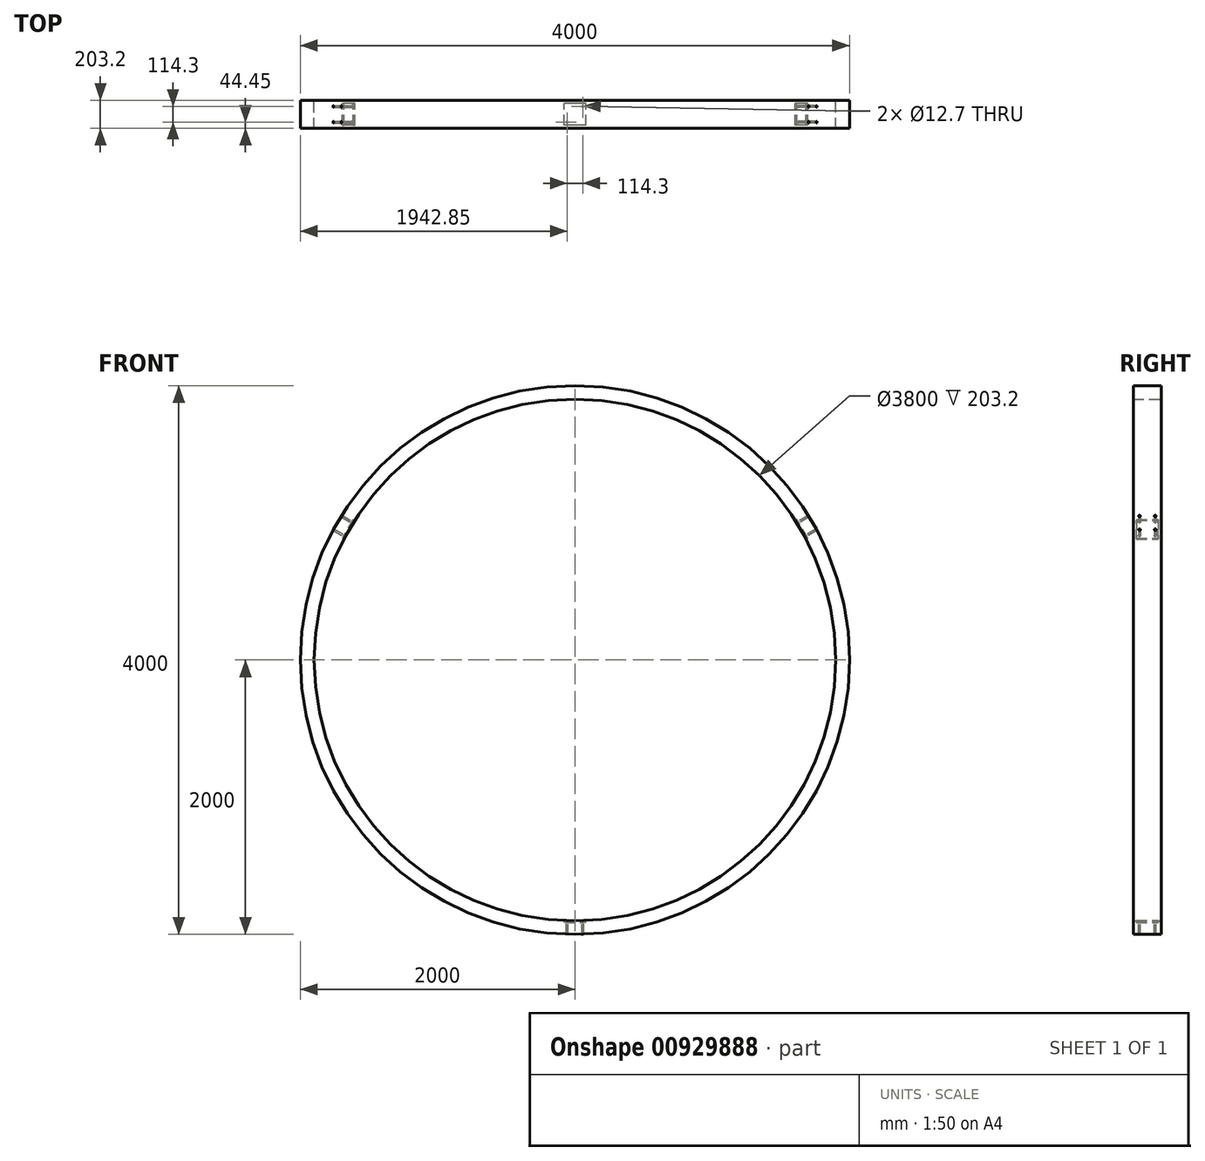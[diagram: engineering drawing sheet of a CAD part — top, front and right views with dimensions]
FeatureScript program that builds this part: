
annotation { "Feature Type Name" : "Feature", "Feature Type Description" : "" }
export const myFeature = defineFeature(function(context is Context, id is Id, definition is map)
    precondition{}
    {
        {
            assignVariable(context, id + "F0", {"name" : "height", "anyValue" : 203.2 * mm});
        }
        {
            var Q0;
            Q0=qCreatedBy(makeId("Front.planeOp"),FACE);
            var sketch = newSketch(context, id + "F1", { "sketchPlane" : qUnion([Q0])});
            skCircle(sketch, "E0", {"center": v(0, 0) * mm, "radius": 1900 * mm});
            skCircle(sketch, "E1", {"center": v(0, 0) * mm, "radius": 2000 * mm});
            skLineSegment(sketch, "E2", {"start": v(0, 0) * mm, "end": v(0, 807.58) * mm, "construction": true});
            skLineSegment(sketch, "E3", {"start": v(0, 1059.46) * mm, "end": v(0, -1141.06) * mm});
            skSolve(sketch);
        }
        {
            var Q0;
            Q0=makeQuery(id+"F1.imprint","IMPRINT",FACE,{"disambiguationData":[TD([[makeQuery(id+"F1.imprint","IMPRINT",EDGE,{"derivedFrom":sQuery(id+"F1.wireOp",EDGE,"E0")}),-1.0]])]});
            extrude(context, id + "F2", {"entities" : qUnion([Q0]), "endBound" : BoundingType.SYMMETRIC, "depth" : getVariable(context, 'height'), "offsetDistance" : 25.4 * mm});
        }
        {
            var Q0;
            Q0=qCreatedBy(makeId("Top.planeOp"),FACE);
            var sketch = newSketch(context, id + "F3", { "sketchPlane" : qUnion([Q0])});
            skLineSegment(sketch, "E4", {"start": v(0, 83.45) * mm, "end": v(0, -223.81) * mm});
            skSolve(sketch);
        }
        {
            var Q0;
            Q0=qCreatedBy(makeId("Top.planeOp"),FACE);
            var Q1;
            Q1=sQuery(id+"F3.wireOp",EDGE,"E4");
            cPlane(context, id + "F4", {"entities" : qUnion([Q0, Q1]), "cplaneType" : CPlaneType.LINE_ANGLE, "offset" : 25.4 * mm, "angle" : 120 * degree, "width" : 152.4 * mm, "height" : 152.4 * mm});
        }
        {
            var Q0;
            Q0=qCreatedBy(makeId("Top.planeOp"),FACE);
            var Q1;
            Q1=sQuery(id+"F3.wireOp",EDGE,"E4");
            cPlane(context, id + "F5", {"entities" : qUnion([Q0, Q1]), "cplaneType" : CPlaneType.LINE_ANGLE, "offset" : 25.4 * mm, "angle" : 240 * degree, "width" : 152.4 * mm, "height" : 152.4 * mm});
        }
        {
            var Q0;
            Q0=qCreatedBy(makeId("Top.planeOp"),FACE);
            var sketch = newSketch(context, id + "F6", { "sketchPlane" : qUnion([Q0])});
            skLineSegment(sketch, "E5.bottom", {"start": v(79.38, -79.38) * mm, "end": v(-79.38, -79.38) * mm});
            skLineSegment(sketch, "E5.top", {"start": v(79.38, 79.38) * mm, "end": v(-79.38, 79.37) * mm});
            skLineSegment(sketch, "E5.left", {"start": v(79.38, -79.38) * mm, "end": v(79.38, 79.38) * mm});
            skLineSegment(sketch, "E5.right", {"start": v(-79.38, -79.38) * mm, "end": v(-79.38, 79.38) * mm});
            skPoint(sketch, "E5.middle", {"position": v(0, 0) * mm});
            skSolve(sketch);
        }
        {
            var Q0;
            Q0=makeQuery(id+"F6.imprint","IMPRINT",FACE,{"disambiguationData":[TD([[makeQuery(id+"F6.imprint","IMPRINT",EDGE,{"derivedFrom":sQuery(id+"F6.wireOp",EDGE,"E5.bottom")}),-1.0]])]});
            var Q1;
            Q1=makeQuery(id+"F2.opExtrude","SWEPT_FACE",FACE,{"disambiguationData":[OSD([sQuery(id+"F1.wireOp",EDGE,"E0")])]});
            extrude(context, id + "F7", {"entities" : qUnion([Q0]), "operationType" : NewBodyOperationType.REMOVE, "endBound" : BoundingType.UP_TO_SURFACE, "oppositeDirection" : true, "depth" : 609.6 * mm, "endBoundEntityFace" : qUnion([Q1]), "hasOffset" : true, "offsetDistance" : 12.7 * mm, "offsetOppositeDirection" : true});
        }
        {
            var Q0;
            Q0=qCreatedBy(id+"F4.planeOp",FACE);
            var sketch = newSketch(context, id + "F8", { "sketchPlane" : qUnion([Q0])});
            skLineSegment(sketch, "E6.bottom", {"start": v(-79.37, -79.37) * mm, "end": v(79.38, -79.37) * mm});
            skLineSegment(sketch, "E6.top", {"start": v(-79.38, 79.38) * mm, "end": v(79.37, 79.38) * mm});
            skLineSegment(sketch, "E6.left", {"start": v(-79.37, -79.37) * mm, "end": v(-79.38, 79.38) * mm});
            skLineSegment(sketch, "E6.right", {"start": v(79.38, -79.37) * mm, "end": v(79.37, 79.38) * mm});
            skPoint(sketch, "E6.middle", {"position": v(0, 0) * mm});
            skSolve(sketch);
        }
        {
            var Q0;
            Q0=qSketchRegion(id+"F8",true);
            var Q1;
            Q1=makeQuery(id+"F2.opExtrude","SWEPT_FACE",FACE,{"disambiguationData":[OSD([sQuery(id+"F1.wireOp",EDGE,"E0")])]});
            extrude(context, id + "F9", {"entities" : qUnion([Q0]), "operationType" : NewBodyOperationType.REMOVE, "endBound" : BoundingType.UP_TO_SURFACE, "depth" : 609.6 * mm, "endBoundEntityFace" : qUnion([Q1]), "hasOffset" : true, "offsetDistance" : 12.7 * mm, "offsetOppositeDirection" : true});
        }
        {
            var Q0;
            Q0=qCreatedBy(id+"F5.planeOp",FACE);
            var sketch = newSketch(context, id + "F10", { "sketchPlane" : qUnion([Q0])});
            skLineSegment(sketch, "E7.bottom", {"start": v(79.38, 79.37) * mm, "end": v(-79.37, 79.37) * mm});
            skLineSegment(sketch, "E7.top", {"start": v(79.37, -79.38) * mm, "end": v(-79.38, -79.38) * mm});
            skLineSegment(sketch, "E7.left", {"start": v(79.38, 79.37) * mm, "end": v(79.37, -79.38) * mm});
            skLineSegment(sketch, "E7.right", {"start": v(-79.37, 79.37) * mm, "end": v(-79.38, -79.38) * mm});
            skPoint(sketch, "E7.middle", {"position": v(0, 0) * mm});
            skSolve(sketch);
        }
        {
            var Q0;
            Q0=qSketchRegion(id+"F10",true);
            var Q1;
            Q1=makeQuery(id+"F2.opExtrude","SWEPT_FACE",FACE,{"disambiguationData":[OSD([sQuery(id+"F1.wireOp",EDGE,"E0")])]});
            extrude(context, id + "F11", {"entities" : qUnion([Q0]), "operationType" : NewBodyOperationType.REMOVE, "endBound" : BoundingType.UP_TO_SURFACE, "depth" : 609.6 * mm, "endBoundEntityFace" : qUnion([Q1]), "hasOffset" : true, "offsetDistance" : 12.7 * mm, "offsetOppositeDirection" : true});
        }
        {
            var Q0;
            Q0=qCreatedBy(id+"F4.planeOp",FACE);
            var sketch = newSketch(context, id + "F12", { "sketchPlane" : qUnion([Q0])});
            skCircle(sketch, "E8", {"center": v(57.15, -57.15) * mm, "radius": 6.35 * mm});
            skCircle(sketch, "E9.MirrorC", {"center": v(57.15, 57.15) * mm, "radius": 6.35 * mm});
            skLineSegment(sketch, "E10", {"start": v(0, -157.36) * mm, "end": v(0, 90.5) * mm, "construction": true});
            skCircle(sketch, "E11.MirrorC", {"center": v(-57.15, -57.15) * mm, "radius": 6.35 * mm});
            skCircle(sketch, "E12.MirrorC", {"center": v(-57.15, 57.15) * mm, "radius": 6.35 * mm});
            skSolve(sketch);
        }
        {
            var Q0;
            Q0=qSketchRegion(id+"F12",true);
            extrude(context, id + "F13", {"entities" : qUnion([Q0]), "operationType" : NewBodyOperationType.REMOVE, "endBound" : BoundingType.THROUGH_ALL, "depth" : 762 * mm, "offsetDistance" : 25.4 * mm});
        }
        {
            var Q0;
            Q0=qCreatedBy(id+"F5.planeOp",FACE);
            var sketch = newSketch(context, id + "F14", { "sketchPlane" : qUnion([Q0])});
            skCircle(sketch, "E13", {"center": v(-57.15, 57.15) * mm, "radius": 6.35 * mm});
            skLineSegment(sketch, "E14", {"start": v(0, 114.48) * mm, "end": v(0, -27.7) * mm, "construction": true});
            skCircle(sketch, "E15.MirrorC", {"center": v(-57.15, -57.15) * mm, "radius": 6.35 * mm});
            skCircle(sketch, "E16.MirrorC", {"center": v(57.15, 57.15) * mm, "radius": 6.35 * mm});
            skCircle(sketch, "E17.MirrorC", {"center": v(57.15, -57.15) * mm, "radius": 6.35 * mm});
            skSolve(sketch);
        }
        {
            var Q0;
            Q0=qSketchRegion(id+"F14",true);
            extrude(context, id + "F15", {"entities" : qUnion([Q0]), "operationType" : NewBodyOperationType.REMOVE, "endBound" : BoundingType.THROUGH_ALL, "depth" : 762 * mm, "offsetDistance" : 25.4 * mm});
        }
        {
            var Q0;
            Q0=qCreatedBy(makeId("Top.planeOp"),FACE);
            var sketch = newSketch(context, id + "F16", { "sketchPlane" : qUnion([Q0])});
            skCircle(sketch, "E18", {"center": v(57.15, 57.15) * mm, "radius": 6.35 * mm});
            skLineSegment(sketch, "E19", {"start": v(124.66, 0) * mm, "end": v(-46.34, 0) * mm, "construction": true});
            skCircle(sketch, "E20.MirrorC", {"center": v(-57.15, 57.15) * mm, "radius": 6.35 * mm});
            skCircle(sketch, "E21.MirrorC", {"center": v(-57.15, -57.15) * mm, "radius": 6.35 * mm});
            skCircle(sketch, "E22.MirrorC", {"center": v(57.15, -57.15) * mm, "radius": 6.35 * mm});
            skSolve(sketch);
        }
        {
            var Q0;
            Q0=makeQuery(id+"F16.imprint","IMPRINT",FACE,{"disambiguationData":[TD([[makeQuery(id+"F16.imprint","IMPRINT",EDGE,{"derivedFrom":sQuery(id+"F16.wireOp",EDGE,"E18")}),1.0]])]});
            var Q1;
            Q1=makeQuery(id+"F16.imprint","IMPRINT",FACE,{"disambiguationData":[TD([[makeQuery(id+"F16.imprint","IMPRINT",EDGE,{"derivedFrom":sQuery(id+"F16.wireOp",EDGE,"E22.MirrorC")}),-1.0]])]});
            var Q2;
            Q2=makeQuery(id+"F16.imprint","IMPRINT",FACE,{"disambiguationData":[TD([[makeQuery(id+"F16.imprint","IMPRINT",EDGE,{"derivedFrom":sQuery(id+"F16.wireOp",EDGE,"E21.MirrorC")}),1.0]])]});
            var Q3;
            Q3=makeQuery(id+"F16.imprint","IMPRINT",FACE,{"disambiguationData":[TD([[makeQuery(id+"F16.imprint","IMPRINT",EDGE,{"derivedFrom":sQuery(id+"F16.wireOp",EDGE,"E20.MirrorC")}),-1.0]])]});
            extrude(context, id + "F17", {"entities" : qUnion([Q0, Q1, Q2, Q3]), "operationType" : NewBodyOperationType.REMOVE, "endBound" : BoundingType.THROUGH_ALL, "oppositeDirection" : true, "depth" : 762 * mm, "offsetDistance" : 25.4 * mm});
        }
    });
